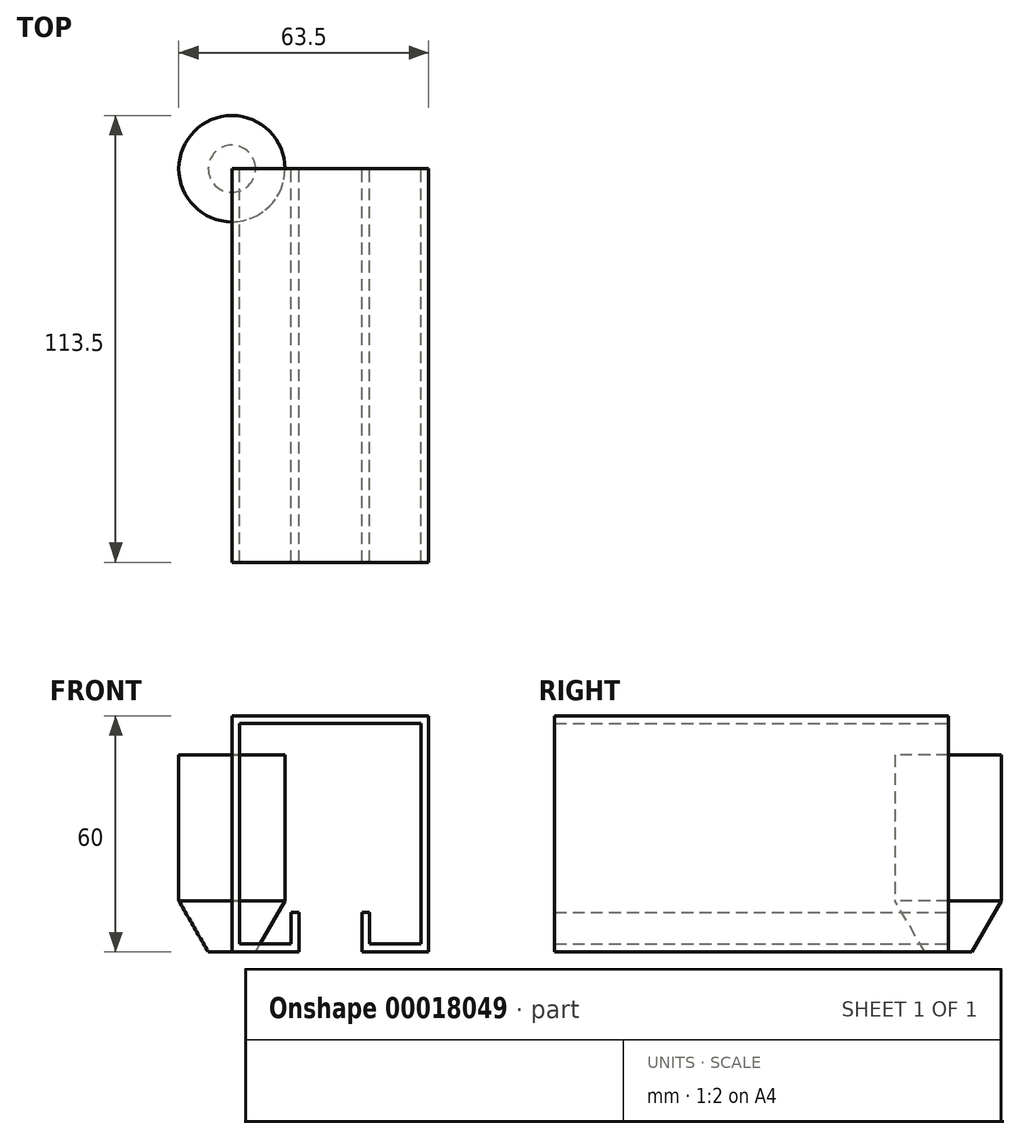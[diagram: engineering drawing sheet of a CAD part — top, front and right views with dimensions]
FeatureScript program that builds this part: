
annotation { "Feature Type Name" : "Feature", "Feature Type Description" : "" }
export const myFeature = defineFeature(function(context is Context, id is Id, definition is map)
    precondition{}
    {
        {
            var Q0;
            Q0=qCreatedBy(makeId("Front.planeOp"),FACE);
            var sketch = newSketch(context, id + "F0", { "sketchPlane" : qUnion([Q0])});
            skLineSegment(sketch, "E0", {"start": v(0, 0) * mm, "end": v(0, 60) * mm});
            skLineSegment(sketch, "E1", {"start": v(0, 60) * mm, "end": v(50, 60) * mm});
            skLineSegment(sketch, "E2", {"start": v(50, 60) * mm, "end": v(50, 0) * mm});
            skLineSegment(sketch, "E3", {"start": v(50, 0) * mm, "end": v(33, 0) * mm});
            skLineSegment(sketch, "E4", {"start": v(33, 0) * mm, "end": v(33, 10) * mm});
            skLineSegment(sketch, "E5", {"start": v(17, 0) * mm, "end": v(17, 10) * mm});
            skLineSegment(sketch, "E6", {"start": v(17, 0) * mm, "end": v(0, 0) * mm});
            skLineSegment(sketch, "E7", {"start": v(17, 10) * mm, "end": v(15, 10) * mm});
            skLineSegment(sketch, "E8", {"start": v(15, 10) * mm, "end": v(15, 2) * mm});
            skLineSegment(sketch, "E9", {"start": v(15, 2) * mm, "end": v(2, 2) * mm});
            skLineSegment(sketch, "E10", {"start": v(2, 2) * mm, "end": v(2, 58) * mm});
            skLineSegment(sketch, "E11", {"start": v(2, 58) * mm, "end": v(48, 58) * mm});
            skLineSegment(sketch, "E12", {"start": v(48, 58) * mm, "end": v(48, 2) * mm});
            skLineSegment(sketch, "E13", {"start": v(48, 2) * mm, "end": v(35, 2) * mm});
            skLineSegment(sketch, "E14", {"start": v(35, 2) * mm, "end": v(35, 10) * mm});
            skLineSegment(sketch, "E15", {"start": v(35, 10) * mm, "end": v(33, 10) * mm});
            skSolve(sketch);
        }
        {
            var Q0;
            Q0=makeQuery(id+"F0.imprint","IMPRINT",FACE,{"disambiguationData":[TD([[makeQuery(id+"F0.imprint","IMPRINT",EDGE,{"derivedFrom":sQuery(id+"F0.wireOp",EDGE,"E0")}),-1.0]])]});
            extrude(context, id + "F1", {"entities" : qUnion([Q0]), "depth" : 100 * mm});
        }
        {
            var Q0;
            Q0=qCreatedBy(makeId("Front.planeOp"),FACE);
            var sketch = newSketch(context, id + "F2", { "sketchPlane" : qUnion([Q0])});
            skLineSegment(sketch, "E16", {"start": v(0, -14.92) * mm, "end": v(0, 108.06) * mm, "construction": true});
            skLineSegment(sketch, "E17", {"start": v(-13.5, 13) * mm, "end": v(-13.5, 50) * mm});
            skLineSegment(sketch, "E18", {"start": v(-13.5, 50) * mm, "end": v(0, 50) * mm});
            skLineSegment(sketch, "E19", {"start": v(-6, 0) * mm, "end": v(0, 0) * mm});
            skLineSegment(sketch, "E20", {"start": v(-6, 0) * mm, "end": v(-13.5, 13) * mm});
            skLineSegment(sketch, "E21", {"start": v(0, 50) * mm, "end": v(0, 0) * mm});
            skSolve(sketch);
        }
        {
            var Q0;
            Q0=makeQuery(id+"F2.imprint","IMPRINT",FACE,{"disambiguationData":[TD([[makeQuery(id+"F2.imprint","IMPRINT",EDGE,{"derivedFrom":sQuery(id+"F2.wireOp",EDGE,"E17")}),-1.0]])]});
            var Q1;
            Q1=sQuery(id+"F2.wireOp",EDGE,"E16");
            revolve(context, id + "F3", {"entities" : qUnion([Q0]), "axis" : qUnion([Q1]), "revolveType" : RevolveType.FULL});
        }
    });
